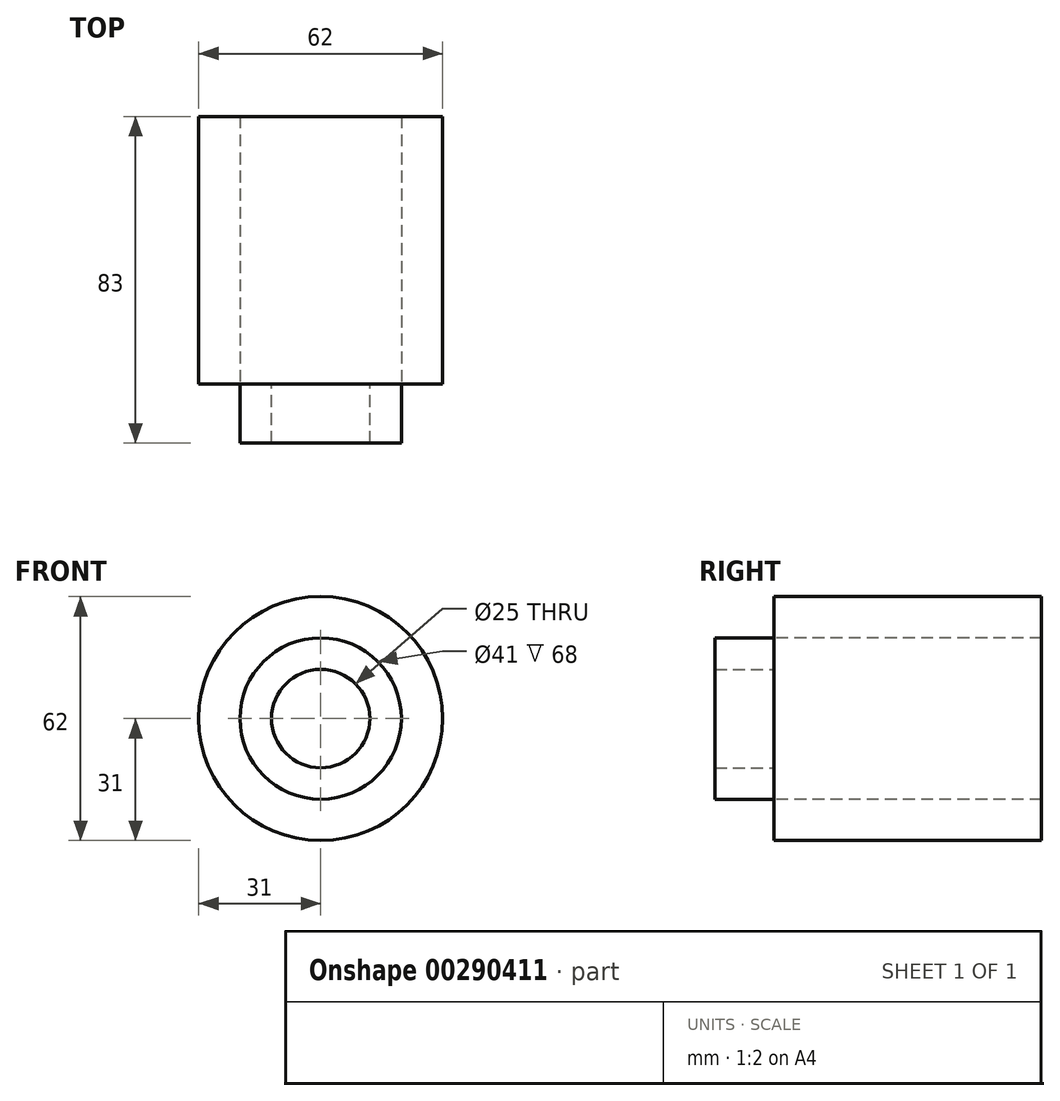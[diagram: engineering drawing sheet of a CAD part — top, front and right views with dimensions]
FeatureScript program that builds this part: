
annotation { "Feature Type Name" : "Feature", "Feature Type Description" : "" }
export const myFeature = defineFeature(function(context is Context, id is Id, definition is map)
    precondition{}
    {
        {
            var Q0;
            Q0=qCreatedBy(makeId("Front.planeOp"),FACE);
            var sketch = newSketch(context, id + "F0", { "sketchPlane" : qUnion([Q0])});
            skCircle(sketch, "E0", {"center": v(0, 0) * mm, "radius": 6 * mm});
            skCircle(sketch, "E1", {"center": v(0, 0) * mm, "radius": 12.5 * mm});
            skCircle(sketch, "E2", {"center": v(0, 0) * mm, "radius": 31 * mm});
            skCircle(sketch, "E3", {"center": v(0, 0) * mm, "radius": 20.5 * mm});
            skSolve(sketch);
        }
        {
            var Q0;
            Q0=makeQuery(id+"F0.imprint","IMPRINT",FACE,{"disambiguationData":[TD([[makeQuery(id+"F0.imprint","IMPRINT",EDGE,{"derivedFrom":sQuery(id+"F0.wireOp",EDGE,"E2")}),1.0]])]});
            extrude(context, id + "F1", {"entities" : qUnion([Q0]), "oppositeDirection" : true, "depth" : 68 * mm});
        }
        {
            var Q0;
            Q0=makeQuery(id+"F0.imprint","IMPRINT",FACE,{"disambiguationData":[TD([[makeQuery(id+"F0.imprint","IMPRINT",EDGE,{"derivedFrom":sQuery(id+"F0.wireOp",EDGE,"E1")}),-1.0]])]});
            extrude(context, id + "F2", {"entities" : qUnion([Q0]), "operationType" : NewBodyOperationType.ADD, "depth" : 15 * mm});
        }
    });
